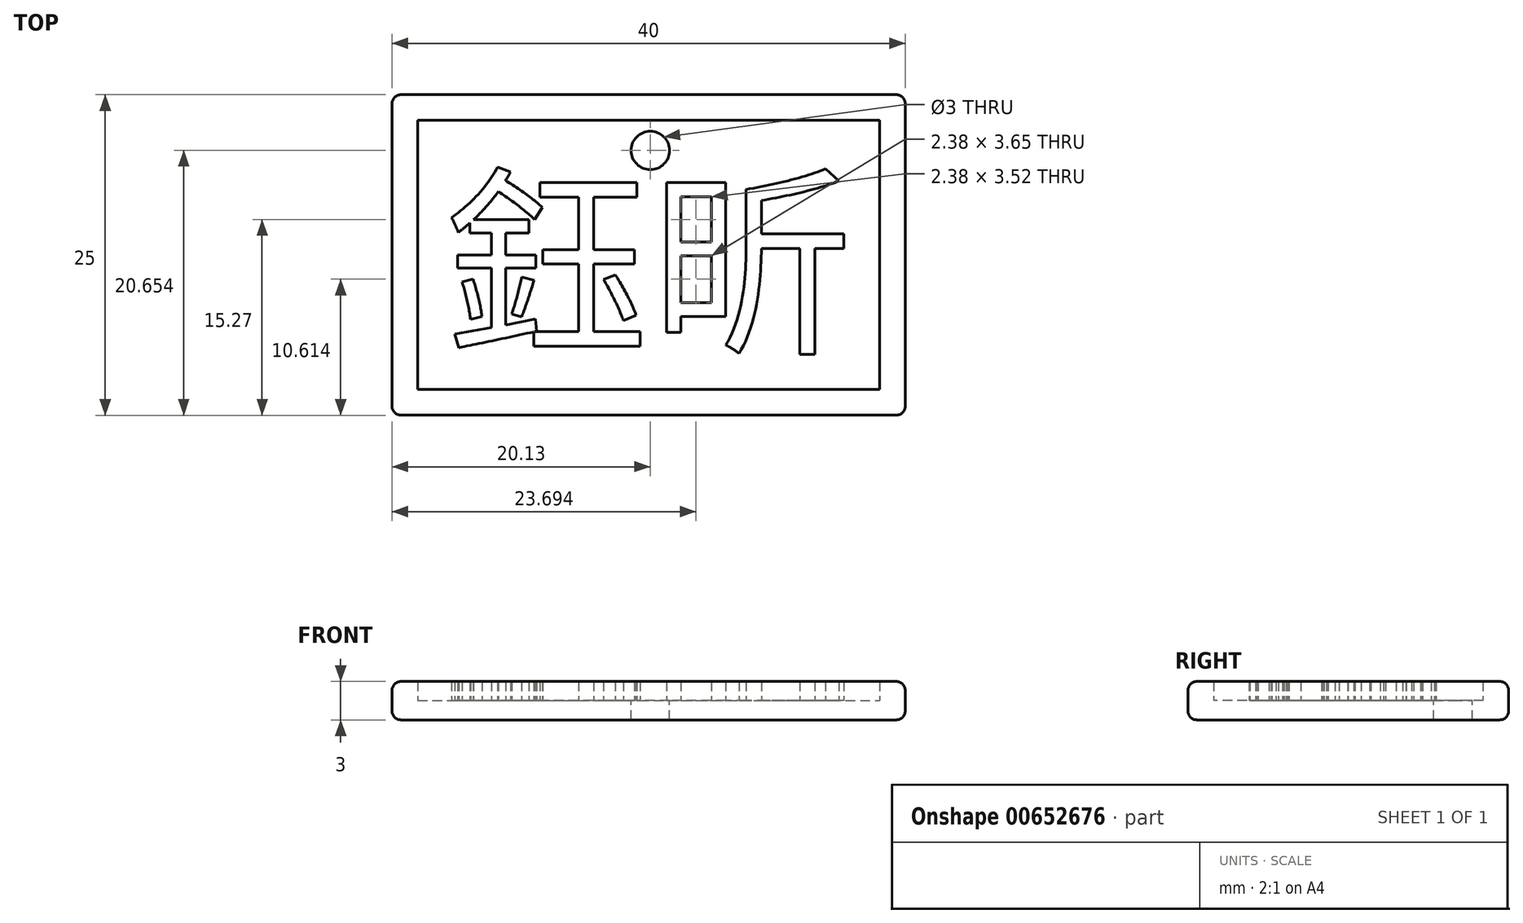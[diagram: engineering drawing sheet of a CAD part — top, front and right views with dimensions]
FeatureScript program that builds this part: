
annotation { "Feature Type Name" : "Feature", "Feature Type Description" : "" }
export const myFeature = defineFeature(function(context is Context, id is Id, definition is map)
    precondition{}
    {
        {
            var Q0;
            Q0=qCreatedBy(makeId("Top.planeOp"),FACE);
            var sketch = newSketch(context, id + "F0", { "sketchPlane" : qUnion([Q0])});
            skLineSegment(sketch, "E0.bottom", {"start": v(-30.1, 14.7) * mm, "end": v(9.9, 14.7) * mm});
            skLineSegment(sketch, "E0.top", {"start": v(-30.1, -10.3) * mm, "end": v(9.9, -10.3) * mm});
            skLineSegment(sketch, "E0.left", {"start": v(-30.1, -10.3) * mm, "end": v(-30.1, 14.7) * mm});
            skLineSegment(sketch, "E0.right", {"start": v(9.9, 14.7) * mm, "end": v(9.9, -10.3) * mm});
            skSolve(sketch);
        }
        {
            var Q0;
            Q0 = qSketchRegion(id + "F0", true);
            extrude(context, id + "F1", {"entities" : qUnion([Q0]), "depth" : 1.5 * mm, "offsetDistance" : 25 * mm});
        }
        {
            var Q0;
            Q0=makeQuery(id+"F1.opExtrude","CAP_FACE",FACE,{"disambiguationData":[OSD([sQuery(id+"F0.wireOp",EDGE,"E0.bottom"),sQuery(id+"F0.wireOp",EDGE,"E0.top"),sQuery(id+"F0.wireOp",EDGE,"E0.left"),sQuery(id+"F0.wireOp",EDGE,"E0.right")])],"isStart":false});
            var sketch = newSketch(context, id + "F2", { "sketchPlane" : qUnion([Q0])});
            skLineSegment(sketch, "E1.bottom", {"start": v(-30.1, 14.7) * mm, "end": v(9.9, 14.7) * mm});
            skLineSegment(sketch, "E1.top", {"start": v(-30.1, -10.3) * mm, "end": v(9.9, -10.3) * mm});
            skLineSegment(sketch, "E1.left", {"start": v(-30.1, 14.7) * mm, "end": v(-30.1, -10.3) * mm});
            skLineSegment(sketch, "E1.right", {"start": v(9.9, 14.7) * mm, "end": v(9.9, -10.3) * mm});
            skLineSegment(sketch, "E2.0", {"start": v(-28.1, 12.7) * mm, "end": v(7.9, 12.7) * mm});
            skLineSegment(sketch, "E2.1", {"start": v(-28.1, 12.7) * mm, "end": v(-28.1, -8.3) * mm});
            skLineSegment(sketch, "E2.2", {"start": v(-28.1, -8.3) * mm, "end": v(7.9, -8.3) * mm});
            skLineSegment(sketch, "E2.3", {"start": v(7.9, 12.7) * mm, "end": v(7.9, -8.3) * mm});
            skSolve(sketch);
        }
        {
            var Q0;
            Q0 = qSketchRegion(id + "F2", true);
            extrude(context, id + "F3", {"entities" : qUnion([Q0]), "operationType" : NewBodyOperationType.ADD, "depth" : 1.5 * mm, "offsetDistance" : 25 * mm});
        }
        {
            var Q0;
            Q0=makeQuery(id+"F1.opExtrude","CAP_FACE",FACE,{"disambiguationData":[OSD([sQuery(id+"F0.wireOp",EDGE,"E0.bottom"),sQuery(id+"F0.wireOp",EDGE,"E0.top"),sQuery(id+"F0.wireOp",EDGE,"E0.left"),sQuery(id+"F0.wireOp",EDGE,"E0.right")])],"isStart":false});
            var sketch = newSketch(context, id + "F4", { "sketchPlane" : qUnion([Q0])});
            skText(sketch, "E3", { "text": "鈺昕", "fontName": "NotoSansCJKtc-Regular.otf"});
            const initialGuessF4  = {"E3": [-0.026, -0.00436, 1, 0, 0.01148]};
            skSetInitialGuess(sketch, initialGuessF4);
            skSolve(sketch);
        }
        {
            var Q0;
            Q0 = qSketchRegion(id + "F4", true);
            extrude(context, id + "F5", {"entities" : qUnion([Q0]), "depth" : 1.5 * mm, "offsetDistance" : 25 * mm});
        }
        {
            var Q0;
            Q0=makeQuery(id+"F1.opExtrude","CAP_FACE",FACE,{"disambiguationData":[OSD([sQuery(id+"F0.wireOp",EDGE,"E0.bottom"),sQuery(id+"F0.wireOp",EDGE,"E0.top"),sQuery(id+"F0.wireOp",EDGE,"E0.left"),sQuery(id+"F0.wireOp",EDGE,"E0.right")])],"isStart":false});
            var sketch = newSketch(context, id + "F6", { "sketchPlane" : qUnion([Q0])});
            skCircle(sketch, "E4", {"center": v(-9.96, 10.34) * mm, "radius": 1.5 * mm});
            skSolve(sketch);
        }
        {
            var Q0;
            Q0 = qSketchRegion(id + "F6", true);
            extrude(context, id + "F7", {"entities" : qUnion([Q0]), "operationType" : NewBodyOperationType.REMOVE, "oppositeDirection" : true, "depth" : 25 * mm, "offsetDistance" : 25 * mm});
        }
        {
            var Q0;
            Q0=makeQuery(id+"F3.opExtrude","CAP_EDGE",EDGE,{"disambiguationData":[OSD([sQuery(id+"F2.wireOp",EDGE,"E1.top")])],"isStart":false});
            var Q1;
            Q1=makeQuery(id+"F1.opExtrude","CAP_EDGE",EDGE,{"disambiguationData":[OSD([sQuery(id+"F0.wireOp",EDGE,"E0.top")])],"isStart":true});
            var Q2;
            Q2=makeQuery(id+"F3.boolean.opBoolean","MERGE",EDGE,{"derivedFrom":[makeQuery(id+"F1.opExtrude","SWEPT_EDGE",EDGE,{"disambiguationData":[OSD([sQuery(id+"F0.wireOp",EDGE,"E0.top"),sQuery(id+"F0.wireOp",EDGE,"E0.left")])]}),makeQuery(id+"F3.opExtrude","SWEPT_EDGE",EDGE,{"disambiguationData":[OSD([sQuery(id+"F2.wireOp",EDGE,"E1.top"),sQuery(id+"F2.wireOp",EDGE,"E1.left")])]})]});
            var Q3;
            Q3=makeQuery(id+"F3.boolean.opBoolean","MERGE",EDGE,{"derivedFrom":[makeQuery(id+"F1.opExtrude","SWEPT_EDGE",EDGE,{"disambiguationData":[OSD([sQuery(id+"F0.wireOp",EDGE,"E0.top"),sQuery(id+"F0.wireOp",EDGE,"E0.right")])]}),makeQuery(id+"F3.opExtrude","SWEPT_EDGE",EDGE,{"disambiguationData":[OSD([sQuery(id+"F2.wireOp",EDGE,"E1.top"),sQuery(id+"F2.wireOp",EDGE,"E1.right")])]})]});
            var Q4;
            Q4=makeQuery(id+"F3.boolean.opBoolean","MERGE",FACE,{"derivedFrom":[makeQuery(id+"F1.opExtrude","SWEPT_FACE",FACE,{"disambiguationData":[OSD([sQuery(id+"F0.wireOp",EDGE,"E0.left")])]}),makeQuery(id+"F3.opExtrude","SWEPT_FACE",FACE,{"disambiguationData":[OSD([sQuery(id+"F2.wireOp",EDGE,"E1.left")])]})]});
            var Q5;
            Q5=makeQuery(id+"F3.boolean.opBoolean","MERGE",FACE,{"derivedFrom":[makeQuery(id+"F1.opExtrude","SWEPT_FACE",FACE,{"disambiguationData":[OSD([sQuery(id+"F0.wireOp",EDGE,"E0.bottom")])]}),makeQuery(id+"F3.opExtrude","SWEPT_FACE",FACE,{"disambiguationData":[OSD([sQuery(id+"F2.wireOp",EDGE,"E1.bottom")])]})]});
            var Q6;
            Q6=makeQuery(id+"F3.boolean.opBoolean","MERGE",FACE,{"derivedFrom":[makeQuery(id+"F1.opExtrude","SWEPT_FACE",FACE,{"disambiguationData":[OSD([sQuery(id+"F0.wireOp",EDGE,"E0.right")])]}),makeQuery(id+"F3.opExtrude","SWEPT_FACE",FACE,{"disambiguationData":[OSD([sQuery(id+"F2.wireOp",EDGE,"E1.right")])]})]});
            fillet(context, id + "F8", {"entities" : qUnion([Q0, Q1, Q2, Q3, Q4, Q5, Q6]), "radius" : 0.7 * mm, "tangentPropagation" : true, "allowEdgeOverflow" : false});
        }
    });
